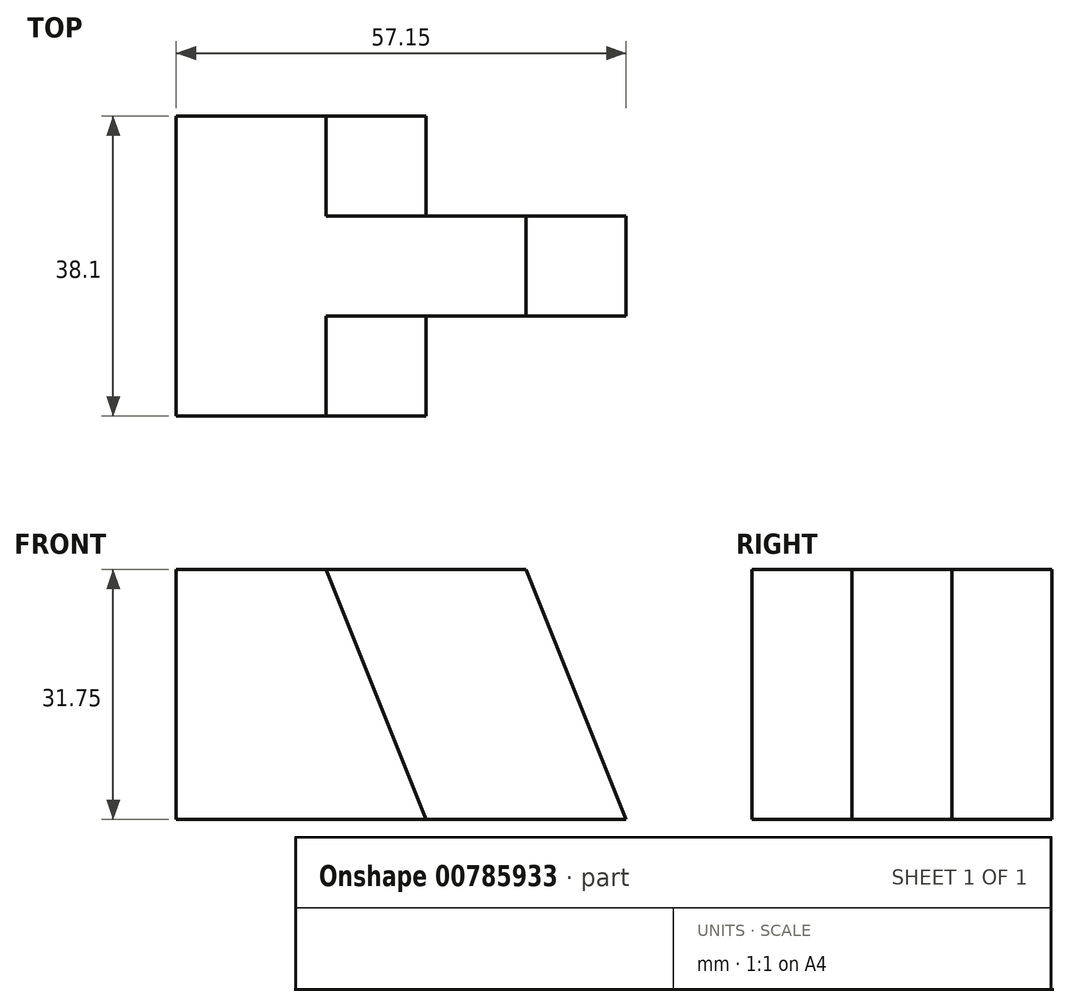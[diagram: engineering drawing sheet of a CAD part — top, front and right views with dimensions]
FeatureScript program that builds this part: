
annotation { "Feature Type Name" : "Feature", "Feature Type Description" : "" }
export const myFeature = defineFeature(function(context is Context, id is Id, definition is map)
    precondition{}
    {
        {
            var Q0;
            Q0=qCreatedBy(makeId("Front.planeOp"),FACE);
            var sketch = newSketch(context, id + "F0", { "sketchPlane" : qUnion([Q0])});
            skLineSegment(sketch, "E0", {"start": v(0, 0) * mm, "end": v(0, 31.75) * mm});
            skLineSegment(sketch, "E1", {"start": v(0, 31.75) * mm, "end": v(57.15, 31.75) * mm});
            skLineSegment(sketch, "E2", {"start": v(57.15, 31.75) * mm, "end": v(57.15, 0) * mm});
            skLineSegment(sketch, "E3", {"start": v(57.15, 0) * mm, "end": v(0, 0) * mm});
            skSolve(sketch);
        }
        {
            var Q0;
            Q0=makeQuery(id+"F0.imprint","IMPRINT",FACE,{"disambiguationData":[TD([[makeQuery(id+"F0.imprint","IMPRINT",EDGE,{"derivedFrom":sQuery(id+"F0.wireOp",EDGE,"E0")}),-1.0]])]});
            extrude(context, id + "F1", {"entities" : qUnion([Q0]), "depth" : 38.1 * mm, "offsetDistance" : 25.4 * mm});
        }
        {
            var Q0;
            Q0=makeQuery(id+"F1.opExtrude","CAP_FACE",FACE,{"disambiguationData":[OSD([sQuery(id+"F0.wireOp",EDGE,"E0"),sQuery(id+"F0.wireOp",EDGE,"E1"),sQuery(id+"F0.wireOp",EDGE,"E2"),sQuery(id+"F0.wireOp",EDGE,"E3")])],"isStart":false});
            var sketch = newSketch(context, id + "F2", { "sketchPlane" : qUnion([Q0])});
            skLineSegment(sketch, "E4", {"start": v(0, 31.75) * mm, "end": v(0, 0) * mm});
            skLineSegment(sketch, "E5", {"start": v(0, 0) * mm, "end": v(31.75, 0) * mm});
            skLineSegment(sketch, "E6", {"start": v(0, 31.75) * mm, "end": v(19.05, 31.75) * mm});
            skLineSegment(sketch, "E7", {"start": v(19.05, 31.75) * mm, "end": v(31.75, 0) * mm});
            skSolve(sketch);
        }
        {
            var Q0;
            {var subQ0=sQuery(id+"F2.wireOp",EDGE,"E7");Q0=makeQuery(id+"F2.imprint","IMPRINT",FACE,{"disambiguationData":[TD([[makeQuery(id+"F2.imprint","IMPRINT",EDGE,{"derivedFrom":subQ0}),1.0]])]});}
            extrude(context, id + "F3", {"entities" : qUnion([Q0]), "operationType" : NewBodyOperationType.REMOVE, "oppositeDirection" : true, "depth" : 12.7 * mm, "offsetDistance" : 25.4 * mm});
        }
        {
            var Q0;
            Q0=makeQuery(id+"F1.opExtrude","CAP_FACE",FACE,{"disambiguationData":[OSD([sQuery(id+"F0.wireOp",EDGE,"E0"),sQuery(id+"F0.wireOp",EDGE,"E1"),sQuery(id+"F0.wireOp",EDGE,"E2"),sQuery(id+"F0.wireOp",EDGE,"E3")])],"isStart":true});
            var sketch = newSketch(context, id + "F4", { "sketchPlane" : qUnion([Q0])});
            skLineSegment(sketch, "E8", {"start": v(0, 31.75) * mm, "end": v(0, 0) * mm});
            skLineSegment(sketch, "E9", {"start": v(0, 0) * mm, "end": v(-31.75, 0) * mm});
            skLineSegment(sketch, "E10", {"start": v(0, 31.75) * mm, "end": v(-19.05, 31.75) * mm});
            skLineSegment(sketch, "E11", {"start": v(-19.05, 31.75) * mm, "end": v(-31.75, 0) * mm});
            skSolve(sketch);
        }
        {
            var Q0;
            {var subQ0=sQuery(id+"F4.wireOp",EDGE,"E11");Q0=makeQuery(id+"F4.imprint","IMPRINT",FACE,{"disambiguationData":[TD([[makeQuery(id+"F4.imprint","IMPRINT",EDGE,{"derivedFrom":subQ0}),-1.0]])]});}
            extrude(context, id + "F5", {"entities" : qUnion([Q0]), "operationType" : NewBodyOperationType.REMOVE, "oppositeDirection" : true, "depth" : 12.7 * mm, "offsetDistance" : 25.4 * mm});
        }
        {
            var Q0;
            Q0=makeQuery(id+"F3.boolean.opBoolean","COPY",FACE,{"derivedFrom":makeQuery(id+"F3.opExtrude","CAP_FACE",FACE,{"disambiguationData":[OSD([sQuery(id+"F0.wireOp",EDGE,"E1"),sQuery(id+"F0.wireOp",EDGE,"E2"),sQuery(id+"F0.wireOp",EDGE,"E3"),sQuery(id+"F2.wireOp",EDGE,"E7")])],"isStart":false})});
            var sketch = newSketch(context, id + "F6", { "sketchPlane" : qUnion([Q0])});
            skLineSegment(sketch, "E12", {"start": v(57.15, 31.75) * mm, "end": v(44.45, 31.75) * mm});
            skLineSegment(sketch, "E13", {"start": v(44.45, 31.75) * mm, "end": v(57.15, 0) * mm});
            skLineSegment(sketch, "E14", {"start": v(57.15, 0) * mm, "end": v(57.15, 31.75) * mm});
            skSolve(sketch);
        }
        {
            var Q0;
            Q0=makeQuery(id+"F6.imprint","IMPRINT",FACE,{"disambiguationData":[TD([[makeQuery(id+"F6.imprint","IMPRINT",EDGE,{"derivedFrom":sQuery(id+"F6.wireOp",EDGE,"E12")}),-1.0]])]});
            extrude(context, id + "F7", {"entities" : qUnion([Q0]), "operationType" : NewBodyOperationType.REMOVE, "oppositeDirection" : true, "depth" : 25.4 * mm, "offsetDistance" : 25.4 * mm});
        }
    });
